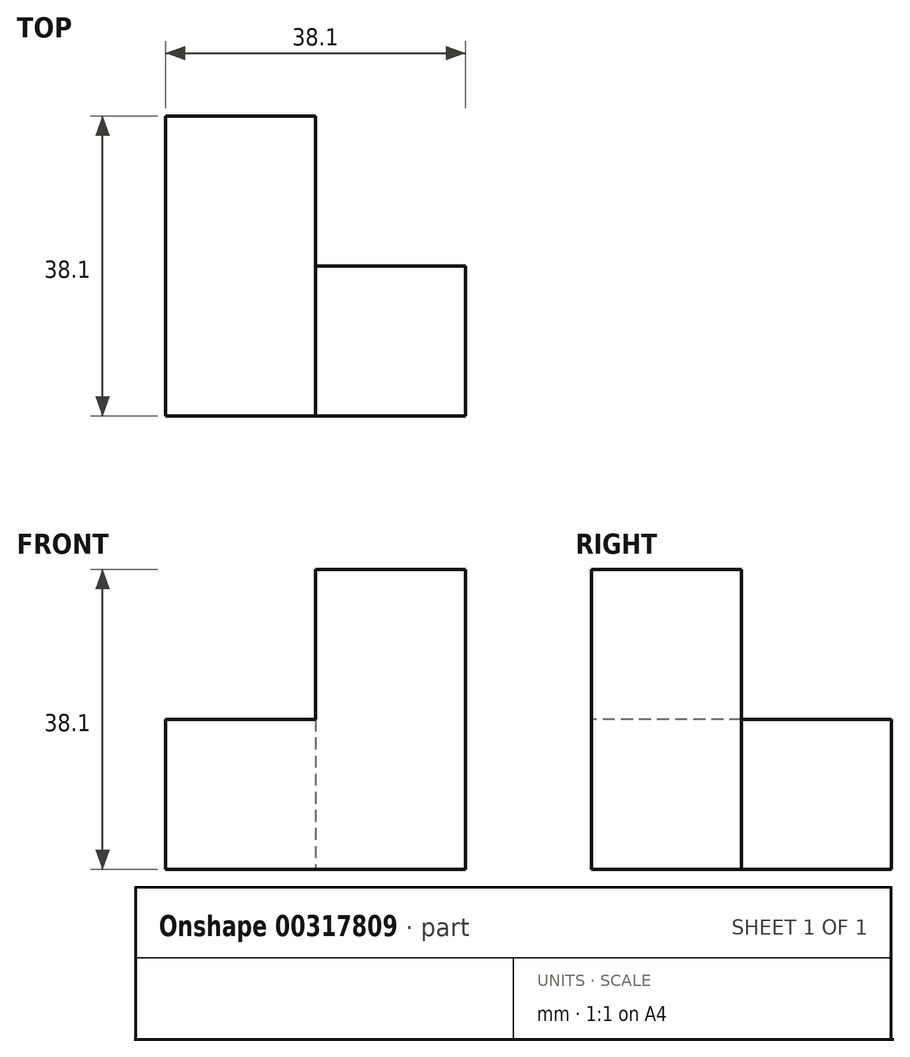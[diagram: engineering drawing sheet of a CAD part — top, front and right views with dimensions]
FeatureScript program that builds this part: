
annotation { "Feature Type Name" : "Feature", "Feature Type Description" : "" }
export const myFeature = defineFeature(function(context is Context, id is Id, definition is map)
    precondition{}
    {
        {
            var Q0;
            Q0=qCreatedBy(makeId("Top.planeOp"),FACE);
            var sketch = newSketch(context, id + "F0", { "sketchPlane" : qUnion([Q0])});
            skLineSegment(sketch, "E0.bottom", {"start": v(0, 0) * mm, "end": v(38.1, 0) * mm});
            skLineSegment(sketch, "E0.top", {"start": v(0, 38.1) * mm, "end": v(19.05, 38.1) * mm});
            skLineSegment(sketch, "E0.left", {"start": v(0, 0) * mm, "end": v(0, 38.1) * mm});
            skLineSegment(sketch, "E0.right", {"start": v(38.1, 0) * mm, "end": v(38.1, 19.05) * mm});
            skLineSegment(sketch, "E1", {"start": v(19.05, 38.1) * mm, "end": v(19.05, 19.05) * mm});
            skLineSegment(sketch, "E2", {"start": v(19.05, 19.05) * mm, "end": v(38.1, 19.05) * mm});
            skPoint(sketch, "E3.orphan", {"position": v(38.1, 38.1) * mm});
            skSolve(sketch);
        }
        {
            var Q0;
            Q0 = qSketchRegion(id + "F0", true);
            extrude(context, id + "F1", {"entities" : qUnion([Q0]), "depth" : 19.05 * mm});
        }
        {
            var Q0;
            Q0=makeQuery(id+"F1.opExtrude","CAP_FACE",FACE,{"disambiguationData":[OSD([sQuery(id+"F0.wireOp",EDGE,"E0.bottom"),sQuery(id+"F0.wireOp",EDGE,"E0.top"),sQuery(id+"F0.wireOp",EDGE,"E0.left"),sQuery(id+"F0.wireOp",EDGE,"E0.right"),sQuery(id+"F0.wireOp",EDGE,"E1"),sQuery(id+"F0.wireOp",EDGE,"E2")])],"isStart":false});
            var sketch = newSketch(context, id + "F2", { "sketchPlane" : qUnion([Q0])});
            skLineSegment(sketch, "E4", {"start": v(19.05, 19.05) * mm, "end": v(19.05, 0) * mm});
            skSolve(sketch);
        }
        {
            var Q0;
            Q0 = qSketchRegion(id + "F2", true);
            var Q1;
            {var subQ0=sQuery(id+"F2.wireOp",EDGE,"E4");Q1=makeQuery(id+"F2.imprint","IMPRINT",FACE,{"disambiguationData":[TD([[makeQuery(id+"F2.imprint","IMPRINT",EDGE,{"derivedFrom":subQ0}),1.0]])]});}
            extrude(context, id + "F3", {"entities" : qUnion([Q0, Q1]), "operationType" : NewBodyOperationType.ADD, "depth" : 19.05 * mm});
        }
    });
